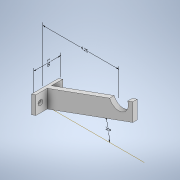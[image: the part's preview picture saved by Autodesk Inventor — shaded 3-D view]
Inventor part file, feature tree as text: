
AUTODESK INVENTOR PART (.ipt)
format: ipt  version: 2021.1 (Build 251245010, 245A)  size: 163,840 bytes
history: native  units: in
note: dims shown in document units (in); Inventor stores cm internally (conversion verified against a paired STEP export)
features: sketch x5, other x4, extrude x4, hole x1
ambient origin geometry x8: Origin, YZ Plane, XZ Plane, XY Plane, X Axis, Y Axis, Z Axis, Center Point
bodies: Solid2 (feature_tree)
feature tree (14):
  other  "Annotations"
  extrude  "Extrusion3"  Depth=0.25in
  extrude  "Extrusion4"  Depth=1.5in
  sketch  "Sketch7"  dims[d26=1.075in d29=0.25in]
  extrude  "Extrusion5"  Depth=0.25in
  hole  "Hole3"  [1 undecoded]
  extrude  "Extrusion6"  TaperAngle=0.0deg  [1 undecoded]
  sketch  "Sketch5"  dims[d21=1.0in d22=0.25in]
  sketch  "Sketch6"  dims[d23=1.5in d24=0.0in d25=0.1374in]
  sketch  "Sketch8"  dims[d30=4.25in d31=0.25in]
  sketch  "Sketch9"  dims[d32=0.0in d33=0.0in d34=0.25in d35=0.25in d47=1.5in d48=0.0in d49=0.15in d50=0.75in d51=0.279in d52=0.25in d53=0.5635in d54=1.0in d55=0.8108in d63=1.5in d64=0.0in d56=0.2085in d57=0.331in d58=1.5in d59=2.3174in d60=0.1374in d62=4.25in]
  other  "Linear Dimension 1"
  other  "Angular Dimension 1"
  other  "Linear Dimension 3"
note: 2 required parameter values undecoded (feature->parameter linkage not recoverable at this tier; creation-order binding heuristic only, values carry confidence <= 0.55)
